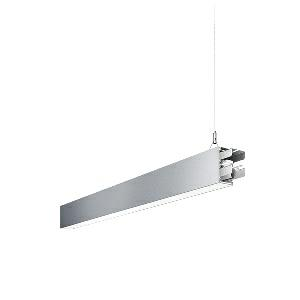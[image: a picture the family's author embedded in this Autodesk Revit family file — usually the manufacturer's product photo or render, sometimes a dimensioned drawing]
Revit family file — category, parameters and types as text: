
# Revit family: idoo_line_-_ilp_3000_830_d_mid_00805727_f99b
name_source: partatom
category: Lighting Fixtures
units: mm (PartAtom-declared; Revit-internal decimal feet)

## family parameters
Cut with Voids When Loaded = No
Host = Face
Light Source = No
Part Type = Normal
Room Calculation Point = No
Round Connector Dimension = Use Diameter
Shared = No

## types (1)
- IDOO.line - ILP 3000/830/D MID (1 x LED, 3000 lm, 3000K)
    Apparent Load = 23 VA
    Approval mark = CE
    CIE Flux Codes = 66 91 98 40 100
    Color Rendering = 80-89
    Color Temperature = 3000K
    Control Gear = Electronic ballast
    Default Elevation = 1800 mm
    Description = ILP 3000/830/D|Suspended luminaire|light source: LED|connected load: 220-240 V, 50/60 Hz|Power consumption: approx. 23 W|standby: approx. 0,20|luminous flux: 3000 lm|luminous efficacy: 130 lm/W|light distribution: Direct/indirect|direct ratio: approx. 40 %|colour temperature: Warm white, ca. 3000 K|color rendering index (CRI): >= 80|chromaticity tolerance:  3 SDCM|System of protection: IP 40|technology: Continuously dimmable|luminaire body|material: Sectional aluminium|colour: Silver|lamp cover: Acrylic (PMMA), Clear|mains lead: 1,0 m With free stranded wires|Fastening: Steel cable 0.3 - 0.7 m|glare control: Prism aperture|luminance(L65): <= 2700 cd/m|unified glare rating(4H 8H): <=  16|special features: DALI Load 1x, TouchDIM - dimming via standard switch, Through-wired, up to 18 m on one mains connection, Flicker-free, Suitable as emergency lighting, Mechanical and electrical connection of the individual modules without tools|
    Frequency = 50 Hz
    Height = 110 mm
    Lamp = 1 x LED
    Lamp Light Flux = 3000 lm
    Lamp count = 1
    Length = 1122 mm
    Luminous efficacy = 130 lm/W
    Manufacturer = Waldmann
    ModVariant = No
    Model = 00805727
    Mounting Place = Ceiling
    Mounting Type = Pendant
    Number of Poles = 1
    OnlyDefault = Yes
    Power Factor = 1
    Product Name = IDOO.line - ILP 3000/830/D MID
    Product group = Suspended luminaire
    ProductGroupID = 9
    Protection Class = Protection class I
    Protection Degree = IP 40
    RLX_Detail_Level = 1
    RLX_Emergency_Light_Flux = 0 lm
    RLX_Emergency_Type = 0
    RLX_Emergency_Type_DB = No
    RlxData = <blob elided: 20893 chars, md5=69fed6d9>
    Socket = socket
    Standby Power = 0 W
    System Light Flux = 3000 lm
    System Power = 23 W
    Type Comments = Product without accessories
    Type Image = 113305000-00692579.jpg
    URL = http://relux.com
    VarID = ---
    Voltage = 230 V
    Voltage Range = 220-240 V
    Weight = 0.00 kg
    Width = 60 mm  [stored 0.19685 ft]

note: [stored X ft] marks values corroborated as IEEE doubles in the binary element streams (Revit-internal decimal feet)

## geometry (parser evidence)
native form markers: Blend x4, Sweep x13
no freeform markers — native parametric forms only
